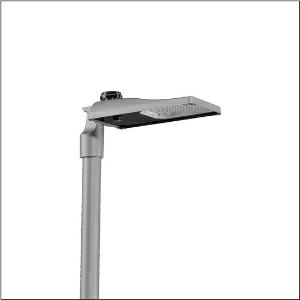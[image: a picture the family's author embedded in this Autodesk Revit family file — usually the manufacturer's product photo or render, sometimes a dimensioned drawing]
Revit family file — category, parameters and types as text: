
# Revit family: streetlight_sl_31_mini___st1_0a_5xh6d35m08ja_363a
name_source: partatom
category: Lighting Fixtures
units: mm (PartAtom-declared; Revit-internal decimal feet)

## family parameters
Cut with Voids When Loaded = No
Host = Face
Light Source = No
Part Type = Normal
Room Calculation Point = No
Round Connector Dimension = Use Diameter
Shared = No

## types (1)
- --- (1 x LED, 12270 lm, 82.5 W, 3000K)
    Apparent Load = 83 VA
    CIE Flux Codes = 40 73 97 100 100
    Color Rendering = 70
    Color Temperature = 3000K
    Default Elevation = 1800 mm
    Description = Streetlight SL 31 mini, mast luminaire, primary light control with lens, of PMMA, primary optical cover: cover, of toughened safety glass, transparent, light distribution: ST1.0a, light emission: direct distribution, primary light characteristic: asymmetric, installation type: post-top, side-entry, LED, High Power LED, rated luminous flux: 12.270lm, luminous efficacy: 149lm/W, light colour: 730, colour temperature: 3000K, control: presetting dimming linear, flexible luminous flux parameterisation, time-dependent luminous flux control, constant luminous flux control, intelligent temperature release in ECG and LED module, overheat protection, with cable H07RN-F 3x 1.5mm², mains connection: 220..240V, AC, 50/60Hz, connection cable pre-assembled, cable length: 10,5m, start of lifetime: 83W, end of service life: 90W, reduction: 37W, luminaire housing, of diecast aluminium, powder-coated, Siteco® metallic grey (DB 702S), corrosivity category C5 high according to DIN EN ISO 12944, no sealing on luminaire upper side, inclination: -15°..+20° (post-top) | -20°..+20° (side-entry), adjustable in 5° steps, mast flange (76/60mm) included as standard, multi-level sealing system, sealing non-destructively replaceable, Smart Interface below, protection rating (complete): IP66, insulation class (complete): insulation class I (protective earthing), certification: CE, ENEC, ENEC+, VDE, UKCA, impact resistance: IK09, permissible operating ambient temperature for outdoor applications: -40..+50°C, standard-compliant lighting for roads and squares, packaging unit: 1 piece

Light Distribution: ST1.0a
    Height = 76 mm
    Lamp = 1 x LED
    Lamp Light Flux = 12270 lm
    Lamp Power = 82.5 W
    Lamp count = 1
    Length = 547 mm
    Luminous efficacy = 149 lm/W
    Manufacturer = Siteco
    ModVariant = No
    Model = 5XH6D35M08JA
    Number of Poles = 1
    OnlyDefault = Yes
    Power Factor = 1
    Product Name = Streetlight SL 31 mini | ST1.0a
    Product group = mast luminaire | pylon top
    ProductGroupID = 6100
    Protection Class = Protection class I
    Protection Degree = IP 66
    RLX_Detail_Level = 1
    RLX_Emergency_Light_Flux = 0 lm
    RLX_Emergency_Type = 0
    RLX_Emergency_Type_DB = No
    RlxData = <blob elided: 40653 chars, md5=9823937f>
    Socket = socket
    Standby Power = 0 W
    System Light Flux = 12270 lm
    System Power = 83 W
    Type Comments = factory setting: luminous flux: 100 % | dim-lin: 254 | 870 mA
    Type Image = l_1300324.jpg
    URL = http://relux.com
    VarID = @adj_007655
    Voltage = 0 V
    Weight = 0.00 kg
    Width = 265 mm

## geometry (parser evidence)
native form markers: Blend x4, Sweep x9
no freeform markers — native parametric forms only
